# Revit family: PRD_AR_WstBns_STRATOSWasteBin_STRX605E
name_source: partatom
category: Specialty Equipment
revit_build: Autodesk Revit 2018 (Build: 20190510_1515(x64)
units: mm (PartAtom-declared; Revit-internal decimal feet)

## family parameters
Cut with Voids When Loaded = Yes
Host = Face
OmniClass Number = 23.40.20.31.11
OmniClass Title = Bins
Part Type = Normal
Room Calculation Point = No
Round Connector Dimension = Use Diameter
Shared = No

## types (1)
- STRX605E
    AssetType = Fixed
    BIMObjectName = PRD_AR_WasteBins_STRATOSWasteBin_STRX605E
    BagHolder = Integrated
    Category = Pr_40_50_07_96, Waste bins
    Default Elevation = 500 mm  [stored 1.64042 ft]
    Description = Waste bin for recessed mounting, stainless steel, surface satin finished, front with InoxPlus surface refinement for the reduction of finger marks and better cleaning characteristics (easy to clean), material thickness 1.5 mm, curved front cover, cylinder lock with KWC standard key, approx. 22 liter capacity, integrated bag holder, includes stainless steel screws and dowels.
    DispenserMaterial = PRD_AR_StainlessSteel_SatinFinished
    DurationUnit = year
    Features = stainless steel, surface satin finished
    FillingVolume = 22.00 liter
    Finish = satin finished
    GrossWeight = 13.26 kg
    IfcExportAs = IfcFurnitureType
    IfcExportType = USERDEFINED
    IntegralAccessories = incl. stainless steel screws and dowels
    IsBuiltIn = TRUE
    Lid = No
    Lock = Key-lock
    MainColor = stainless steel
    Manufacturer = KWC Group AG
    ManufacturerName = KWC Group AG
    ManufacturerURL = www.kwc.com
    Material = stainless steel
    MaterialCode = 1.4301
    MaterialThickness = 1.50 mm
    Model = STRX605E
    ModelNumber = 2000057229
    ModelReference = STRX605E
    NBSDescription = Waste bins
    NBSReference = 45-35-72/380
    Name = Waste Bin STRX605E
    NetWeight = 10.65 kg
    NominalDepth = 202 mm  [stored 0.66273 ft]
    NominalHeight = 862 mm  [stored 2.82808 ft]
    NominalWidth = 327 mm
    Offset = 0 mm  [stored 0 ft]
    ProductInformation = https://pim.kwc.com
    Size = 327 x 862 x 202 mm
    Style = Waste bin
    SurfaceTreatment = InoxPlus (anti fingerprint)
    TypeOfFixing = Screw
    TypeOfMounting = Recessed mounting
    URL = www.kwc.com
    Uniclass2015Code = Pr_40_50_07_96
    Uniclass2015Title = Waste bins
    Uniclass2015Version = Products v1.17
    Version = 1
    WarrantyDurationUnit = year

note: [stored X ft] marks values corroborated as IEEE doubles in the binary element streams (Revit-internal decimal feet)

## geometry (parser evidence)
native form markers: Sweep x4
no freeform markers — native parametric forms only
